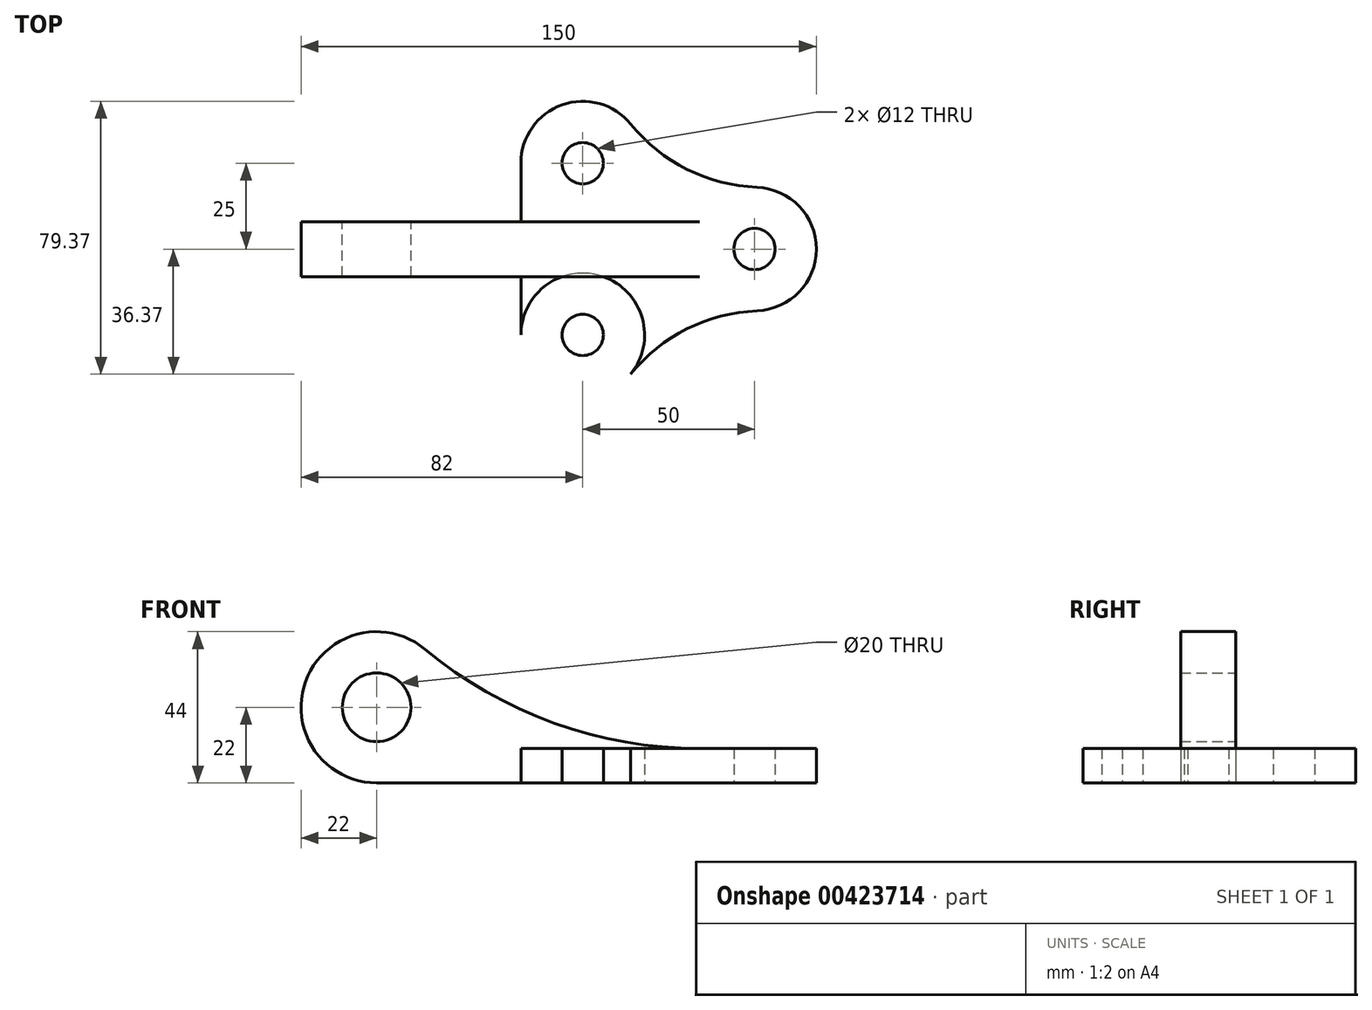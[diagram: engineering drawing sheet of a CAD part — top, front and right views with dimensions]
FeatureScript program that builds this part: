
annotation { "Feature Type Name" : "Feature", "Feature Type Description" : "" }
export const myFeature = defineFeature(function(context is Context, id is Id, definition is map)
    precondition{}
    {
        {
            var Q0;
            Q0=qCreatedBy(makeId("Top.planeOp"),FACE);
            var sketch = newSketch(context, id + "F0", { "sketchPlane" : qUnion([Q0])});
            skCircle(sketch, "E0", {"center": v(0, 0) * mm, "radius": 6 * mm});
            skCircle(sketch, "E1", {"center": v(-50, 25) * mm, "radius": 6 * mm});
            skCircle(sketch, "E2.MirrorC", {"center": v(-50, -25) * mm, "radius": 6 * mm});
            skCircle(sketch, "E3", {"center": v(0, 0) * mm, "radius": 18 * mm});
            skCircle(sketch, "E4", {"center": v(-50, 25) * mm, "radius": 18 * mm});
            skCircle(sketch, "E5", {"center": v(-50, -25) * mm, "radius": 18 * mm});
            skArc(sketch, "E6", {"start": v(0.72, -17.99) * mm, "mid": v(-19.64, -23.22) * mm, "end": v(-36.04, -36.37) * mm});
            skLineSegment(sketch, "E7", {"start": v(-68, -25) * mm, "end": v(-68, 25) * mm});
            skArc(sketch, "E8.MirrorCS", {"start": v(0.72, 17.99) * mm, "mid": v(-19.64, 23.22) * mm, "end": v(-36.04, 36.37) * mm});
            skSolve(sketch);
        }
        {
            var Q0;
            {var subQ0=sQuery(id+"F0.wireOp",EDGE,"E6");Q0=makeQuery(id+"F0.imprint","IMPRINT",FACE,{"disambiguationData":[TD([[makeQuery(id+"F0.imprint","IMPRINT",EDGE,{"derivedFrom":subQ0}),-1.0]])]});}
            var Q1;
            Q1=makeQuery(id+"F0.imprint","IMPRINT",FACE,{"disambiguationData":[TD([[makeQuery(id+"F0.imprint","IMPRINT",EDGE,{"derivedFrom":sQuery(id+"F0.wireOp",EDGE,"E1")}),-1.0]])]});
            var Q2;
            Q2=makeQuery(id+"F0.imprint","IMPRINT",FACE,{"disambiguationData":[TD([[makeQuery(id+"F0.imprint","IMPRINT",EDGE,{"derivedFrom":sQuery(id+"F0.wireOp",EDGE,"E0")}),-1.0]])]});
            var Q3;
            Q3=makeQuery(id+"F0.imprint","IMPRINT",FACE,{"disambiguationData":[TD([[makeQuery(id+"F0.imprint","IMPRINT",EDGE,{"derivedFrom":sQuery(id+"F0.wireOp",EDGE,"E2.MirrorC")}),1.0]])]});
            extrude(context, id + "F1", {"entities" : qUnion([Q0, Q1, Q2, Q3]), "depth" : 10 * mm});
        }
        {
            var Q0;
            Q0=qCreatedBy(makeId("Front.planeOp"),FACE);
            var sketch = newSketch(context, id + "F2", { "sketchPlane" : qUnion([Q0])});
            skLineSegment(sketch, "E9", {"start": v(0, 0) * mm, "end": v(-110, 0) * mm});
            skLineSegment(sketch, "E10", {"start": v(-110, 0) * mm, "end": v(-110, 81.5) * mm, "construction": true});
            skCircle(sketch, "E11", {"center": v(-110, 22) * mm, "radius": 22 * mm});
            skCircle(sketch, "E12", {"center": v(-110, 22) * mm, "radius": 10 * mm});
            skLineSegment(sketch, "E13.0", {"start": v(-68, 10) * mm, "end": v(-36.04, 10) * mm});
            skLineSegment(sketch, "E14.0", {"start": v(0.72, 10) * mm, "end": v(-36.04, 10) * mm});
            skLineSegment(sketch, "E15", {"start": v(18, 10) * mm, "end": v(18, 0) * mm});
            skArc(sketch, "E16", {"start": v(-95.93, 38.91) * mm, "mid": v(-58.49, 17.45) * mm, "end": v(-15.98, 10) * mm});
            skLineSegment(sketch, "E17", {"start": v(-68, 10) * mm, "end": v(-68, 0) * mm});
            skSolve(sketch);
        }
        {
            var Q0;
            {var subQ0=sQuery(id+"F2.wireOp",EDGE,"E13.0");Q0=makeQuery(id+"F2.imprint","IMPRINT",FACE,{"disambiguationData":[TD([[makeQuery(id+"F2.imprint","IMPRINT",EDGE,{"derivedFrom":subQ0}),1.0]])]});}
            var Q1;
            Q1=makeQuery(id+"F2.imprint","IMPRINT",FACE,{"disambiguationData":[TD([[makeQuery(id+"F2.imprint","IMPRINT",EDGE,{"derivedFrom":sQuery(id+"F2.wireOp",EDGE,"E12")}),-1.0]])]});
            extrude(context, id + "F3", {"entities" : qUnion([Q0, Q1]), "operationType" : NewBodyOperationType.ADD, "endBound" : BoundingType.SYMMETRIC, "depth" : 16 * mm});
        }
    });
